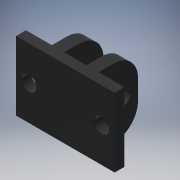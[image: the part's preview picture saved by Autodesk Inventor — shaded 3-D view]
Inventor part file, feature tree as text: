
AUTODESK INVENTOR PART (.ipt)
format: ipt  version: 2016 (Build 200138000, 138)  size: 165,376 bytes
history: native  units: mm
features: extrude x3, sketch x3, fillet x1
ambient origin geometry x8: Origin, YZ Plane, XZ Plane, XY Plane, X Axis, Y Axis, Z Axis, Center Point
bodies: Solid1 (feature_tree)
feature tree (7):
  extrude  "Extrusion1"  Depth=2.5mm
  extrude  "Extrusion2"  Depth=20.0mm
  fillet  "Fillet1"  Radius=5.25mm
  extrude  "Extrusion3"  Depth=14.0mm
  sketch  "Sketch1"  dims[d0=4.5mm d3=2.5mm]
  sketch  "Sketch2"  dims[d5=2.5mm d7=20.0mm d8=5.25mm]
  sketch  "Sketch3"  dims[d9=5.25mm d10=14.0mm d11=3.0mm d12=3.0mm d13=2.0mm d14=0.0mm d16=4.5mm d17=2.5mm d18=2.5mm d19=8.0mm d20=0.0mm d21=5.0mm d23=3.0mm d24=5.0mm d25=20.0mm d26=0.0mm d27=2.625mm d28=2.625mm d29=2.625mm]
